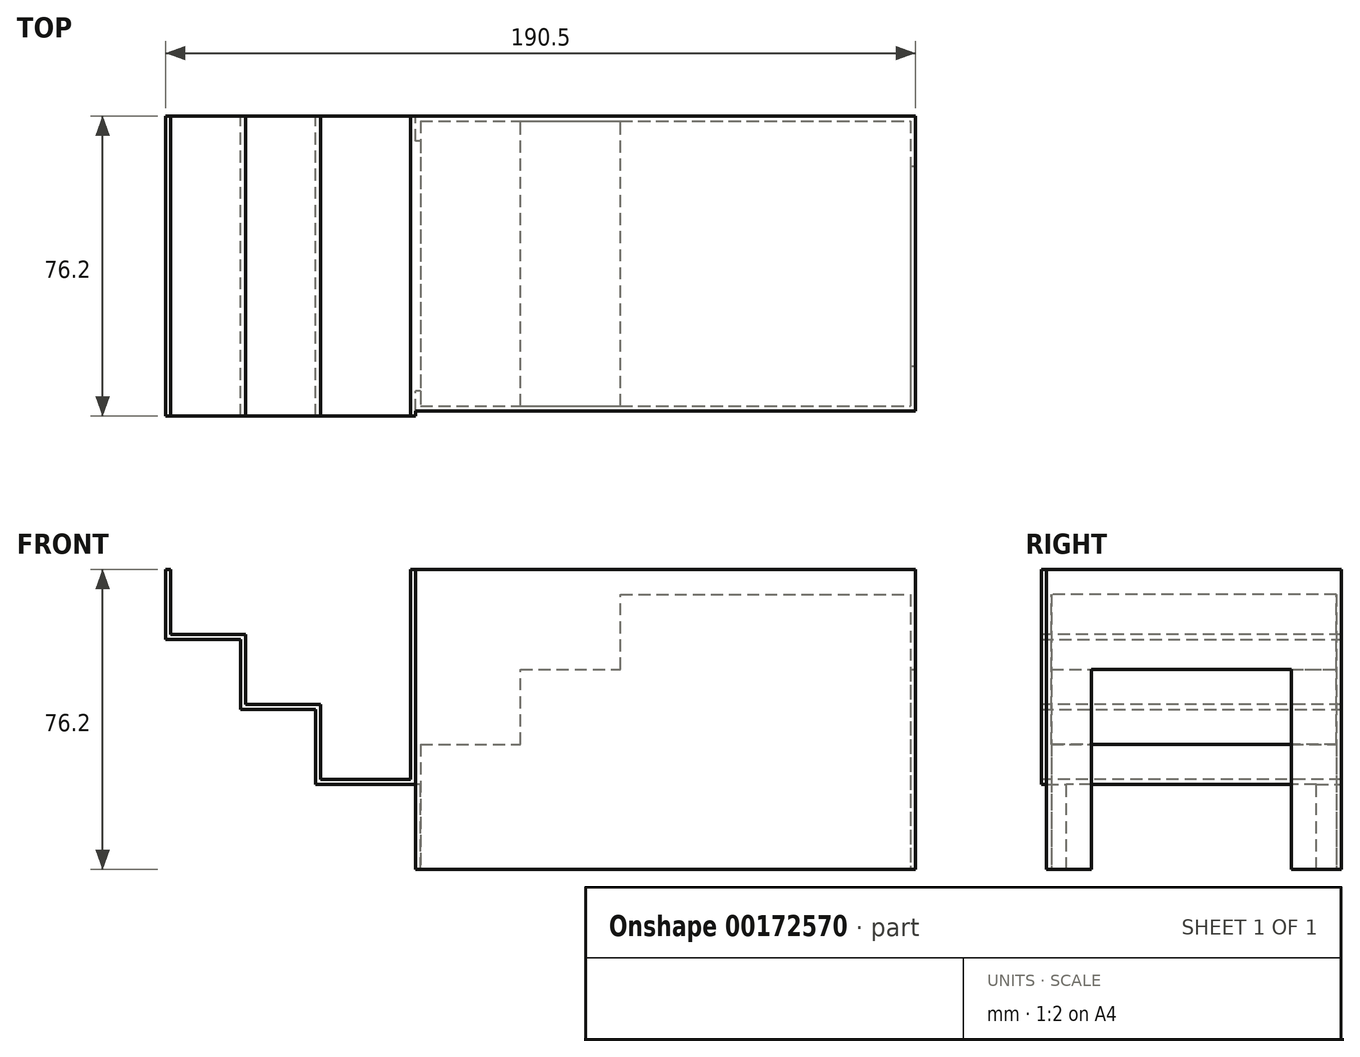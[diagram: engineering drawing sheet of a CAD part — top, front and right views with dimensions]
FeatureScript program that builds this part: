
annotation { "Feature Type Name" : "Feature", "Feature Type Description" : "" }
export const myFeature = defineFeature(function(context is Context, id is Id, definition is map)
    precondition{}
    {
        {
            var Q0;
            Q0=qCreatedBy(makeId("Front.planeOp"),FACE);
            var sketch = newSketch(context, id + "F0", { "sketchPlane" : qUnion([Q0])});
            skLineSegment(sketch, "E0.bottom", {"start": v(0, 0) * mm, "end": v(127, 0) * mm});
            skLineSegment(sketch, "E0.top", {"start": v(0, 76.2) * mm, "end": v(127, 76.2) * mm});
            skLineSegment(sketch, "E0.left", {"start": v(0, 0) * mm, "end": v(0, 76.2) * mm});
            skLineSegment(sketch, "E0.right", {"start": v(127, 0) * mm, "end": v(127, 76.2) * mm});
            skSolve(sketch);
        }
        {
            var Q0;
            Q0=makeQuery(id+"F0.imprint","IMPRINT",FACE,{"disambiguationData":[TD([[makeQuery(id+"F0.imprint","IMPRINT",EDGE,{"derivedFrom":sQuery(id+"F0.wireOp",EDGE,"E0.bottom")}),1.0]])]});
            extrude(context, id + "F1", {"entities" : qUnion([Q0]), "depth" : 74.93 * mm});
        }
        {
            var Q0;
            Q0=makeQuery(id+"F1.opExtrude","SWEPT_FACE",FACE,{"disambiguationData":[OSD([sQuery(id+"F0.wireOp",EDGE,"E0.bottom")])]});
            var sketch = newSketch(context, id + "F2", { "sketchPlane" : qUnion([Q0])});
            skLineSegment(sketch, "E1.bottom", {"start": v(1.27, 1.27) * mm, "end": v(125.73, 1.27) * mm});
            skLineSegment(sketch, "E1.top", {"start": v(1.27, 73.66) * mm, "end": v(125.73, 73.66) * mm});
            skLineSegment(sketch, "E1.left", {"start": v(1.27, 1.27) * mm, "end": v(1.27, 73.66) * mm});
            skLineSegment(sketch, "E1.right", {"start": v(125.73, 1.27) * mm, "end": v(125.73, 73.66) * mm});
            skSolve(sketch);
        }
        {
            var Q0;
            Q0=makeQuery(id+"F2.imprint","IMPRINT",FACE,{"disambiguationData":[TD([[makeQuery(id+"F2.imprint","IMPRINT",EDGE,{"derivedFrom":sQuery(id+"F2.wireOp",EDGE,"E1.bottom")}),1.0]])]});
            extrude(context, id + "F3", {"entities" : qUnion([Q0]), "operationType" : NewBodyOperationType.REMOVE, "oppositeDirection" : true, "depth" : 69.85 * mm});
        }
        {
            var Q0;
            Q0=makeQuery(id+"F1.opExtrude","SWEPT_FACE",FACE,{"disambiguationData":[OSD([sQuery(id+"F0.wireOp",EDGE,"E0.left")])]});
            var sketch = newSketch(context, id + "F4", { "sketchPlane" : qUnion([Q0])});
            skLineSegment(sketch, "E2.bottom", {"start": v(76.2, 76.2) * mm, "end": v(0, 76.2) * mm});
            skLineSegment(sketch, "E2.top", {"start": v(76.2, 21.6) * mm, "end": v(0, 21.59) * mm});
            skLineSegment(sketch, "E2.left", {"start": v(76.2, 76.2) * mm, "end": v(76.2, 21.6) * mm});
            skLineSegment(sketch, "E2.right", {"start": v(0, 76.2) * mm, "end": v(0, 21.59) * mm});
            skSolve(sketch);
        }
        {
            var Q0;
            Q0=makeQuery(id+"F4.imprint","IMPRINT",FACE,{"disambiguationData":[TD([[makeQuery(id+"F4.imprint","IMPRINT",EDGE,{"derivedFrom":sQuery(id+"F4.wireOp",EDGE,"E2.bottom")}),1.0]])]});
            extrude(context, id + "F5", {"entities" : qUnion([Q0]), "operationType" : NewBodyOperationType.ADD, "depth" : 25.4 * mm});
        }
        {
            var Q0;
            Q0=makeQuery(id+"F5.opExtrude","CAP_FACE",FACE,{"disambiguationData":[OSD([sQuery(id+"F4.wireOp",EDGE,"E2.bottom"),sQuery(id+"F4.wireOp",EDGE,"E2.top"),sQuery(id+"F4.wireOp",EDGE,"E2.left"),sQuery(id+"F4.wireOp",EDGE,"E2.right")])],"isStart":false});
            var sketch = newSketch(context, id + "F6", { "sketchPlane" : qUnion([Q0])});
            skLineSegment(sketch, "E3.bottom", {"start": v(76.2, 76.2) * mm, "end": v(0, 76.2) * mm});
            skLineSegment(sketch, "E3.top", {"start": v(76.2, 40.64) * mm, "end": v(0, 40.64) * mm});
            skLineSegment(sketch, "E3.left", {"start": v(76.2, 76.2) * mm, "end": v(76.2, 40.64) * mm});
            skLineSegment(sketch, "E3.right", {"start": v(0, 76.2) * mm, "end": v(0, 40.64) * mm});
            skSolve(sketch);
        }
        {
            var Q0;
            Q0=makeQuery(id+"F6.imprint","IMPRINT",FACE,{"disambiguationData":[TD([[makeQuery(id+"F6.imprint","IMPRINT",EDGE,{"derivedFrom":sQuery(id+"F6.wireOp",EDGE,"E3.bottom")}),1.0]])]});
            extrude(context, id + "F7", {"entities" : qUnion([Q0]), "operationType" : NewBodyOperationType.ADD, "depth" : 19.05 * mm});
        }
        {
            var Q0;
            Q0=makeQuery(id+"F7.opExtrude","CAP_FACE",FACE,{"disambiguationData":[OSD([sQuery(id+"F6.wireOp",EDGE,"E3.bottom"),sQuery(id+"F6.wireOp",EDGE,"E3.top"),sQuery(id+"F6.wireOp",EDGE,"E3.left"),sQuery(id+"F6.wireOp",EDGE,"E3.right")])],"isStart":false});
            var sketch = newSketch(context, id + "F8", { "sketchPlane" : qUnion([Q0])});
            skLineSegment(sketch, "E4.bottom", {"start": v(76.2, 76.2) * mm, "end": v(0, 76.2) * mm});
            skLineSegment(sketch, "E4.top", {"start": v(76.2, 58.42) * mm, "end": v(0, 58.42) * mm});
            skLineSegment(sketch, "E4.left", {"start": v(76.2, 76.2) * mm, "end": v(76.2, 58.42) * mm});
            skLineSegment(sketch, "E4.right", {"start": v(0, 76.2) * mm, "end": v(0, 58.42) * mm});
            skSolve(sketch);
        }
        {
            var Q0;
            Q0=makeQuery(id+"F8.imprint","IMPRINT",FACE,{"disambiguationData":[TD([[makeQuery(id+"F8.imprint","IMPRINT",EDGE,{"derivedFrom":sQuery(id+"F8.wireOp",EDGE,"E4.bottom")}),1.0]])]});
            extrude(context, id + "F9", {"entities" : qUnion([Q0]), "operationType" : NewBodyOperationType.ADD, "depth" : 19.05 * mm});
        }
        {
            var Q0;
            Q0=makeQuery(id+"F3.boolean.opBoolean","COPY",FACE,{"derivedFrom":makeQuery(id+"F3.opExtrude","CAP_FACE",FACE,{"disambiguationData":[OSD([sQuery(id+"F2.wireOp",EDGE,"E1.bottom"),sQuery(id+"F2.wireOp",EDGE,"E1.top"),sQuery(id+"F2.wireOp",EDGE,"E1.left"),sQuery(id+"F2.wireOp",EDGE,"E1.right")])],"isStart":false})});
            var sketch = newSketch(context, id + "F10", { "sketchPlane" : qUnion([Q0])});
            skLineSegment(sketch, "E5.bottom", {"start": v(1.27, 73.66) * mm, "end": v(52.07, 73.66) * mm});
            skLineSegment(sketch, "E5.top", {"start": v(1.27, 1.27) * mm, "end": v(52.07, 1.27) * mm});
            skLineSegment(sketch, "E5.left", {"start": v(1.27, 73.66) * mm, "end": v(1.27, 1.27) * mm});
            skLineSegment(sketch, "E5.right", {"start": v(52.07, 73.66) * mm, "end": v(52.07, 1.27) * mm});
            skSolve(sketch);
        }
        {
            var Q0;
            Q0=makeQuery(id+"F1.opExtrude","SWEPT_FACE",FACE,{"disambiguationData":[OSD([sQuery(id+"F0.wireOp",EDGE,"E0.left")])]});
            var sketch = newSketch(context, id + "F11", { "sketchPlane" : qUnion([Q0])});
            skLineSegment(sketch, "E6.bottom", {"start": v(6.35, 21.59) * mm, "end": v(69.85, 21.59) * mm});
            skLineSegment(sketch, "E6.top", {"start": v(6.35, -34.45) * mm, "end": v(69.85, -34.45) * mm});
            skLineSegment(sketch, "E6.left", {"start": v(6.35, 21.59) * mm, "end": v(6.35, -34.45) * mm});
            skLineSegment(sketch, "E6.right", {"start": v(69.85, 21.59) * mm, "end": v(69.85, -34.45) * mm});
            skSolve(sketch);
        }
        {
            var Q0;
            {var subQ0=sQuery(id+"F11.wireOp",EDGE,"E6.top");Q0=makeQuery(id+"F11.imprint","IMPRINT",FACE,{"disambiguationData":[TD([[makeQuery(id+"F11.imprint","IMPRINT",EDGE,{"derivedFrom":subQ0}),1.0]])]});}
            var Q1;
            {var subQ0=sQuery(id+"F11.wireOp",EDGE,"E6.bottom");Q1=makeQuery(id+"F11.imprint","IMPRINT",FACE,{"disambiguationData":[TD([[makeQuery(id+"F11.imprint","IMPRINT",EDGE,{"derivedFrom":subQ0}),1.0]])]});}
            extrude(context, id + "F12", {"entities" : qUnion([Q0, Q1]), "operationType" : NewBodyOperationType.REMOVE, "oppositeDirection" : true, "depth" : 25.4 * mm});
        }
        {
            var Q0;
            Q0=makeQuery(id+"F10.imprint","IMPRINT",FACE,{"disambiguationData":[TD([[makeQuery(id+"F10.imprint","IMPRINT",EDGE,{"derivedFrom":sQuery(id+"F10.wireOp",EDGE,"E5.bottom")}),-1.0]])]});
            extrude(context, id + "F13", {"entities" : qUnion([Q0]), "operationType" : NewBodyOperationType.ADD, "depth" : 19.05 * mm});
        }
        {
            var Q0;
            Q0=makeQuery(id+"F13.opExtrude","CAP_FACE",FACE,{"disambiguationData":[OSD([sQuery(id+"F10.wireOp",EDGE,"E5.bottom"),sQuery(id+"F10.wireOp",EDGE,"E5.top"),sQuery(id+"F10.wireOp",EDGE,"E5.left"),sQuery(id+"F10.wireOp",EDGE,"E5.right")])],"isStart":false});
            var sketch = newSketch(context, id + "F14", { "sketchPlane" : qUnion([Q0])});
            skLineSegment(sketch, "E7.bottom", {"start": v(1.27, 73.66) * mm, "end": v(26.67, 73.66) * mm});
            skLineSegment(sketch, "E7.top", {"start": v(1.27, 1.27) * mm, "end": v(26.67, 1.27) * mm});
            skLineSegment(sketch, "E7.left", {"start": v(1.27, 73.66) * mm, "end": v(1.27, 1.27) * mm});
            skLineSegment(sketch, "E7.right", {"start": v(26.67, 73.66) * mm, "end": v(26.67, 1.27) * mm});
            skSolve(sketch);
        }
        {
            var Q0;
            Q0=makeQuery(id+"F14.imprint","IMPRINT",FACE,{"disambiguationData":[TD([[makeQuery(id+"F14.imprint","IMPRINT",EDGE,{"derivedFrom":sQuery(id+"F14.wireOp",EDGE,"E7.bottom")}),-1.0]])]});
            extrude(context, id + "F15", {"entities" : qUnion([Q0]), "operationType" : NewBodyOperationType.ADD, "depth" : 19.05 * mm});
        }
        {
            var Q0;
            Q0=makeQuery(id+"F9.boolean.opBoolean","MERGE",FACE,{"derivedFrom":[makeQuery(id+"F7.boolean.opBoolean","MERGE",FACE,{"derivedFrom":[makeQuery(id+"F5.boolean.opBoolean","MERGE",FACE,{"derivedFrom":[makeQuery(id+"F1.opExtrude","CAP_FACE",FACE,{"disambiguationData":[OSD([sQuery(id+"F0.wireOp",EDGE,"E0.bottom"),sQuery(id+"F0.wireOp",EDGE,"E0.top"),sQuery(id+"F0.wireOp",EDGE,"E0.left"),sQuery(id+"F0.wireOp",EDGE,"E0.right")])],"isStart":false}),makeQuery(id+"F5.opExtrude","SWEPT_FACE",FACE,{"disambiguationData":[OSD([sQuery(id+"F4.wireOp",EDGE,"E2.left")])]})]}),makeQuery(id+"F7.opExtrude","SWEPT_FACE",FACE,{"disambiguationData":[OSD([sQuery(id+"F6.wireOp",EDGE,"E3.left")])]})]}),makeQuery(id+"F9.opExtrude","SWEPT_FACE",FACE,{"disambiguationData":[OSD([sQuery(id+"F8.wireOp",EDGE,"E4.left")])]})]});
            var sketch = newSketch(context, id + "F16", { "sketchPlane" : qUnion([Q0])});
            skLineSegment(sketch, "E8", {"start": v(-1.27, 76.2) * mm, "end": v(-1.27, 22.86) * mm});
            skLineSegment(sketch, "E9", {"start": v(-1.27, 22.86) * mm, "end": v(-24.13, 22.86) * mm});
            skLineSegment(sketch, "E10", {"start": v(-24.13, 22.86) * mm, "end": v(-24.13, 41.91) * mm});
            skLineSegment(sketch, "E11", {"start": v(-24.13, 41.91) * mm, "end": v(-43.18, 41.91) * mm});
            skLineSegment(sketch, "E12", {"start": v(-43.18, 41.91) * mm, "end": v(-43.18, 59.7) * mm});
            skLineSegment(sketch, "E13", {"start": v(-43.18, 59.7) * mm, "end": v(-62.23, 59.7) * mm});
            skLineSegment(sketch, "E14", {"start": v(-62.23, 59.7) * mm, "end": v(-62.23, 76.2) * mm});
            skLineSegment(sketch, "E15", {"start": v(-1.27, 76.2) * mm, "end": v(-10.71, 76.2) * mm});
            skLineSegment(sketch, "E16", {"start": v(-62.23, 76.2) * mm, "end": v(-1.27, 76.2) * mm});
            skSolve(sketch);
        }
        {
            var Q0;
            {var subQ0=sQuery(id+"F16.wireOp",EDGE,"E8");Q0=makeQuery(id+"F16.imprint","IMPRINT",FACE,{"disambiguationData":[TD([[makeQuery(id+"F16.imprint","IMPRINT",EDGE,{"derivedFrom":subQ0}),-1.0]])]});}
            extrude(context, id + "F17", {"entities" : qUnion([Q0]), "operationType" : NewBodyOperationType.REMOVE, "oppositeDirection" : true, "depth" : 76.2 * mm});
        }
        {
            var Q0;
            Q0=makeQuery(id+"F1.opExtrude","SWEPT_FACE",FACE,{"disambiguationData":[OSD([sQuery(id+"F0.wireOp",EDGE,"E0.right")])]});
            var sketch = newSketch(context, id + "F18", { "sketchPlane" : qUnion([Q0])});
            skLineSegment(sketch, "E17.bottom", {"start": v(-12.7, 50.8) * mm, "end": v(-63.5, 50.8) * mm});
            skLineSegment(sketch, "E17.top", {"start": v(-12.7, -33.03) * mm, "end": v(-63.5, -33.03) * mm});
            skLineSegment(sketch, "E17.left", {"start": v(-12.7, 50.8) * mm, "end": v(-12.7, -33.03) * mm});
            skLineSegment(sketch, "E17.right", {"start": v(-63.5, 50.8) * mm, "end": v(-63.5, -33.03) * mm});
            skSolve(sketch);
        }
        {
            var Q0;
            {var subQ0=sQuery(id+"F18.wireOp",EDGE,"E17.top");Q0=makeQuery(id+"F18.imprint","IMPRINT",FACE,{"disambiguationData":[TD([[makeQuery(id+"F18.imprint","IMPRINT",EDGE,{"derivedFrom":subQ0}),-1.0]])]});}
            var Q1;
            {var subQ0=sQuery(id+"F18.wireOp",EDGE,"E17.bottom");Q1=makeQuery(id+"F18.imprint","IMPRINT",FACE,{"disambiguationData":[TD([[makeQuery(id+"F18.imprint","IMPRINT",EDGE,{"derivedFrom":subQ0}),1.0]])]});}
            extrude(context, id + "F19", {"entities" : qUnion([Q0, Q1]), "operationType" : NewBodyOperationType.REMOVE, "oppositeDirection" : true, "depth" : 25.4 * mm});
        }
    });
